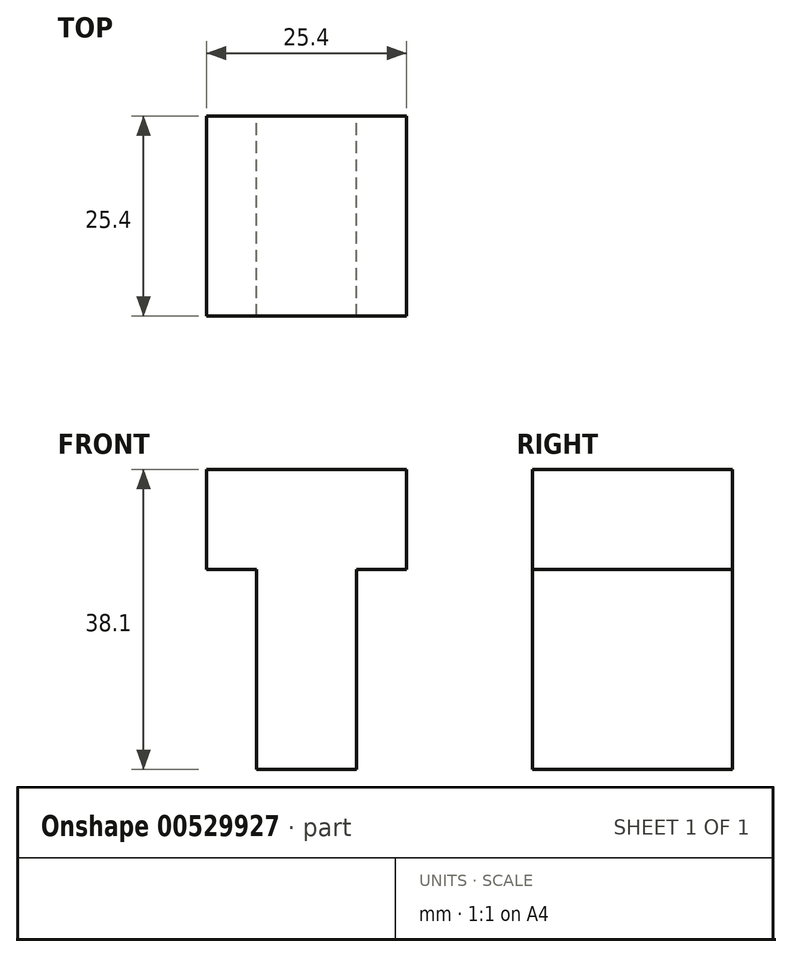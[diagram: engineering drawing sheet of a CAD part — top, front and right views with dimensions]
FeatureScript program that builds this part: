
annotation { "Feature Type Name" : "Feature", "Feature Type Description" : "" }
export const myFeature = defineFeature(function(context is Context, id is Id, definition is map)
    precondition{}
    {
        {
            var Q0;
            Q0=qCreatedBy(makeId("Front.planeOp"),FACE);
            var sketch = newSketch(context, id + "F0", { "sketchPlane" : qUnion([Q0])});
            skLineSegment(sketch, "E0", {"start": v(-19.05, 30.16) * mm, "end": v(6.35, 30.16) * mm});
            skLineSegment(sketch, "E1", {"start": v(-19.05, 30.16) * mm, "end": v(-19.05, 17.46) * mm});
            skLineSegment(sketch, "E2", {"start": v(6.35, 30.16) * mm, "end": v(6.35, 17.46) * mm});
            skLineSegment(sketch, "E3", {"start": v(-19.05, 17.46) * mm, "end": v(-12.7, 17.46) * mm});
            skLineSegment(sketch, "E4", {"start": v(6.35, 17.46) * mm, "end": v(0, 17.46) * mm});
            skLineSegment(sketch, "E5", {"start": v(-12.7, 17.46) * mm, "end": v(-12.7, -7.94) * mm});
            skLineSegment(sketch, "E6", {"start": v(0, 17.46) * mm, "end": v(0, -7.94) * mm});
            skLineSegment(sketch, "E7", {"start": v(-12.7, -7.94) * mm, "end": v(0, -7.94) * mm});
            skSolve(sketch);
        }
        {
            var Q0;
            Q0=makeQuery(id+"F0.imprint","IMPRINT",FACE,{"disambiguationData":[TD([[makeQuery(id+"F0.imprint","IMPRINT",EDGE,{"derivedFrom":sQuery(id+"F0.wireOp",EDGE,"E0")}),-1.0]])]});
            extrude(context, id + "F1", {"entities" : qUnion([Q0]), "depth" : 25.4 * mm, "offsetDistance" : 25.4 * mm});
        }
    });
